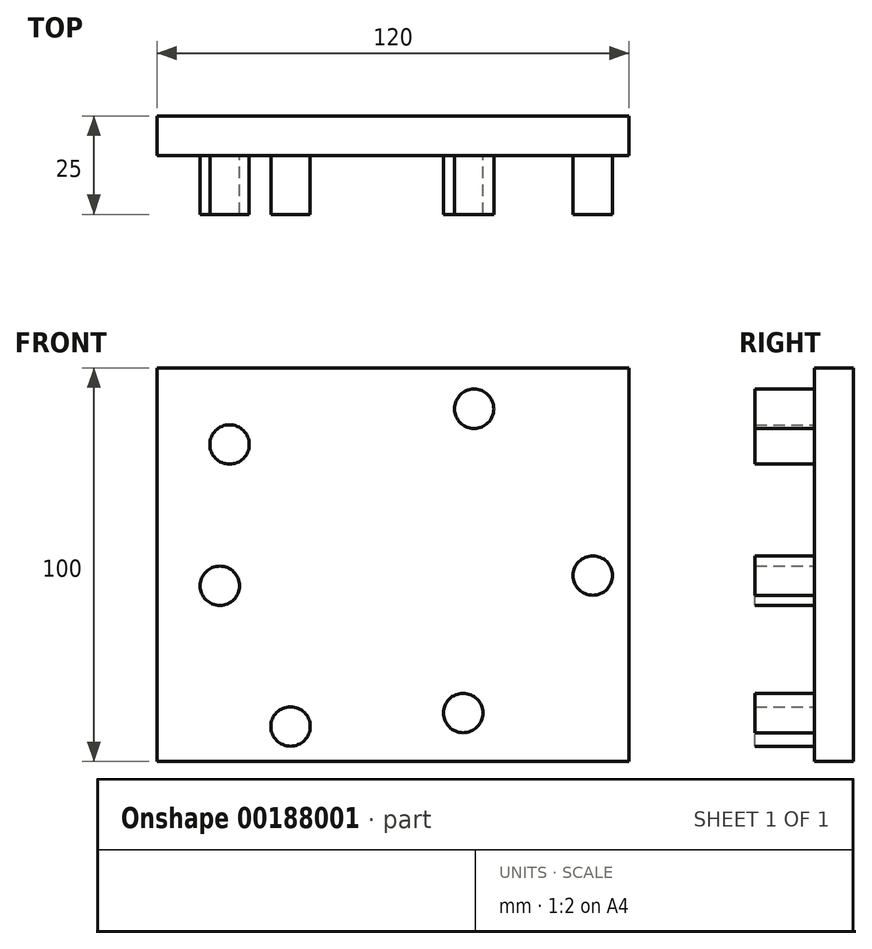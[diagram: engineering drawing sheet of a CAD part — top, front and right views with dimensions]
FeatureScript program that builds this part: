
annotation { "Feature Type Name" : "Feature", "Feature Type Description" : "" }
export const myFeature = defineFeature(function(context is Context, id is Id, definition is map)
    precondition{}
    {
        {
            var Q0;
            Q0=qCreatedBy(makeId("Front.planeOp"),FACE);
            var sketch = newSketch(context, id + "F0", { "sketchPlane" : qUnion([Q0])});
            skLineSegment(sketch, "E0.bottom", {"start": v(60, 50) * mm, "end": v(-60, 50) * mm});
            skLineSegment(sketch, "E0.top", {"start": v(60, -50) * mm, "end": v(-60, -50) * mm});
            skLineSegment(sketch, "E0.left", {"start": v(60, 50) * mm, "end": v(60, -50) * mm});
            skLineSegment(sketch, "E0.right", {"start": v(-60, 50) * mm, "end": v(-60, -50) * mm});
            skPoint(sketch, "E0.middle", {"position": v(0, 0) * mm});
            skSolve(sketch);
        }
        {
            var Q0;
            Q0=makeQuery(id+"F0.imprint","IMPRINT",FACE,{"disambiguationData":[TD([[makeQuery(id+"F0.imprint","IMPRINT",EDGE,{"derivedFrom":sQuery(id+"F0.wireOp",EDGE,"E0.bottom")}),1.0]])]});
            extrude(context, id + "F1", {"entities" : qUnion([Q0]), "depth" : 10 * mm});
        }
        {
            var Q0;
            Q0=makeQuery(id+"F1.opExtrude","CAP_FACE",FACE,{"disambiguationData":[OSD([sQuery(id+"F0.wireOp",EDGE,"E0.bottom"),sQuery(id+"F0.wireOp",EDGE,"E0.top"),sQuery(id+"F0.wireOp",EDGE,"E0.left"),sQuery(id+"F0.wireOp",EDGE,"E0.right")])],"isStart":false});
            var sketch = newSketch(context, id + "F2", { "sketchPlane" : qUnion([Q0])});
            skCircle(sketch, "E1", {"center": v(-41.52, 30.55) * mm, "radius": 5 * mm});
            skCircle(sketch, "E2", {"center": v(-43.99, -5.36) * mm, "radius": 5 * mm});
            skCircle(sketch, "E3", {"center": v(-26.03, -41.1) * mm, "radius": 5 * mm});
            skCircle(sketch, "E4", {"center": v(17.83, -37.68) * mm, "radius": 5 * mm});
            skCircle(sketch, "E5", {"center": v(50.76, -2.75) * mm, "radius": 5 * mm});
            skCircle(sketch, "E6", {"center": v(20.6, 39.6) * mm, "radius": 5 * mm});
            skSolve(sketch);
        }
        {
            var Q0;
            Q0=qSketchRegion(id+"F2",true);
            extrude(context, id + "F3", {"entities" : qUnion([Q0]), "operationType" : NewBodyOperationType.ADD, "depth" : 15 * mm});
        }
    });
